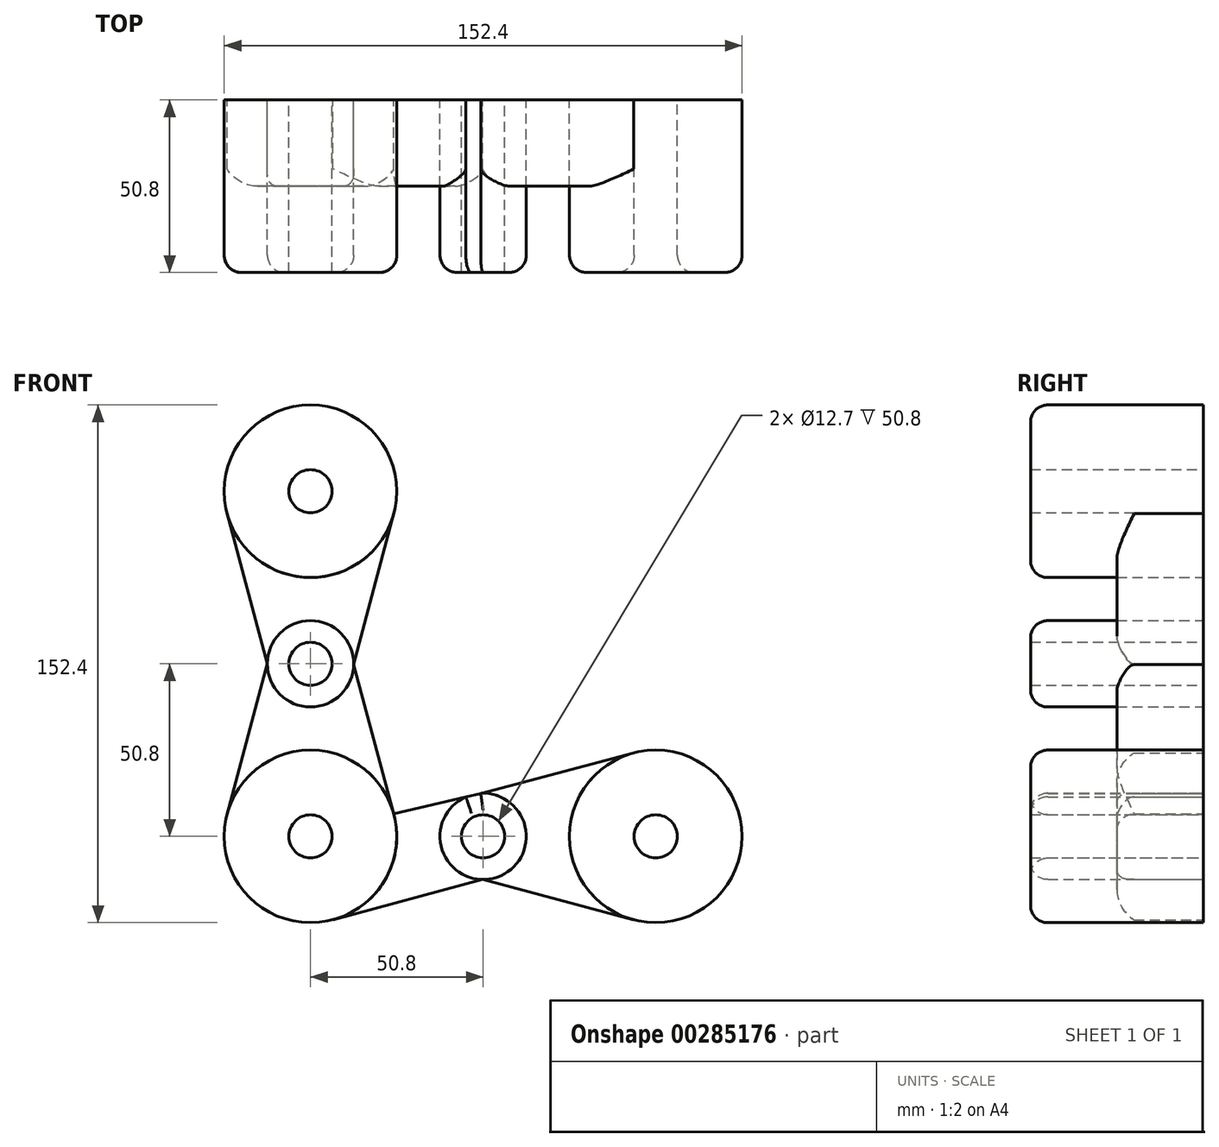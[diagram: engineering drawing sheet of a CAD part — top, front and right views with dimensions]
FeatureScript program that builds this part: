
annotation { "Feature Type Name" : "Feature", "Feature Type Description" : "" }
export const myFeature = defineFeature(function(context is Context, id is Id, definition is map)
    precondition{}
    {
        {
            var Q0;
            Q0=qCreatedBy(makeId("Front.planeOp"),FACE);
            var sketch = newSketch(context, id + "F0", { "sketchPlane" : qUnion([Q0])});
            skLineSegment(sketch, "E0", {"start": v(-86.7, -63.44) * mm, "end": v(-35.9, -63.44) * mm});
            skLineSegment(sketch, "E1", {"start": v(-35.9, -63.44) * mm, "end": v(14.9, -63.44) * mm});
            skPoint(sketch, "E1.endSnap0", {"position": v(-61.3, -63.44) * mm});
            skLineSegment(sketch, "E2", {"start": v(-86.7, -63.44) * mm, "end": v(-86.7, -12.64) * mm});
            skLineSegment(sketch, "E3", {"start": v(-86.7, -12.64) * mm, "end": v(-86.7, 38.16) * mm});
            skCircle(sketch, "E4", {"center": v(-86.7, 38.16) * mm, "radius": 25.4 * mm});
            skCircle(sketch, "E5", {"center": v(-86.7, -63.44) * mm, "radius": 25.4 * mm});
            skCircle(sketch, "E6", {"center": v(14.9, -63.44) * mm, "radius": 25.4 * mm});
            skCircle(sketch, "E7", {"center": v(-86.7, -12.64) * mm, "radius": 12.7 * mm});
            skCircle(sketch, "E8", {"center": v(-35.9, -63.44) * mm, "radius": 12.7 * mm});
            skLineSegment(sketch, "E9", {"start": v(-99.4, -12.64) * mm, "end": v(-111.23, -56.88) * mm});
            skLineSegment(sketch, "E10", {"start": v(-99.4, -12.64) * mm, "end": v(-111.23, 31.6) * mm});
            skLineSegment(sketch, "E11", {"start": v(-74, -12.86) * mm, "end": v(-62.17, -56.84) * mm});
            skLineSegment(sketch, "E12", {"start": v(-36.03, -76.14) * mm, "end": v(-80.1, -87.97) * mm});
            skLineSegment(sketch, "E13", {"start": v(-36.03, -76.14) * mm, "end": v(8.36, -87.98) * mm});
            skLineSegment(sketch, "E14", {"start": v(-74, -12.86) * mm, "end": v(-62.15, 31.62) * mm});
            skLineSegment(sketch, "E15", {"start": v(-36.6, -50.76) * mm, "end": v(8.43, -38.88) * mm});
            skLineSegment(sketch, "E16", {"start": v(-62.17, -56.84) * mm, "end": v(-36.6, -50.76) * mm});
            skSolve(sketch);
        }
        {
            var Q0;
            {var subQ0=sQuery(id+"F0.wireOp",EDGE,"E4");var subQ1=makeQuery(id+"F0.imprint","INTERSECT",VERTEX,{"derivedFrom":[subQ0,sQuery(id+"F0.wireOp",EDGE,"E10")]});Q0=makeQuery(id+"F0.imprint","IMPRINT",FACE,{"disambiguationData":[TD([[makeQuery(id+"F0.imprint","IMPRINT",EDGE,{"disambiguationData":[TD([[subQ1,-1.0]])],"derivedFrom":subQ0}),1.0]])]});}
            var Q1;
            {var subQ0=sQuery(id+"F0.wireOp",EDGE,"E3");var subQ1=sQuery(id+"F0.wireOp",EDGE,"E2");var subQ2=makeQuery(id+"F0.imprint","INTERSECT",VERTEX,{"derivedFrom":[subQ1,subQ0]});Q1=makeQuery(id+"F0.imprint","IMPRINT",FACE,{"disambiguationData":[TD([[makeQuery(id+"F0.imprint","IMPRINT",EDGE,{"disambiguationData":[TD([[subQ2,1.0]])],"derivedFrom":subQ1}),-1.0]])]});}
            var Q2;
            {var subQ0=sQuery(id+"F0.wireOp",EDGE,"E3");var subQ1=sQuery(id+"F0.wireOp",EDGE,"E2");var subQ2=makeQuery(id+"F0.imprint","INTERSECT",VERTEX,{"derivedFrom":[subQ1,subQ0]});Q2=makeQuery(id+"F0.imprint","IMPRINT",FACE,{"disambiguationData":[TD([[makeQuery(id+"F0.imprint","IMPRINT",EDGE,{"disambiguationData":[TD([[subQ2,1.0]])],"derivedFrom":subQ1}),1.0]])]});}
            var Q3;
            {var subQ3=sQuery(id+"F0.wireOp",EDGE,"E2");var subQ4=sQuery(id+"F0.wireOp",EDGE,"E0");var subQ5=makeQuery(id+"F0.imprint","INTERSECT",VERTEX,{"derivedFrom":[subQ4,subQ3]});Q3=makeQuery(id+"F0.imprint","IMPRINT",FACE,{"disambiguationData":[TD([[makeQuery(id+"F0.imprint","IMPRINT",EDGE,{"disambiguationData":[TD([[subQ5,-1.0]])],"derivedFrom":subQ4}),-1.0]])]});}
            var Q4;
            {var subQ0=sQuery(id+"F0.wireOp",EDGE,"E2");var subQ1=sQuery(id+"F0.wireOp",EDGE,"E0");var subQ2=makeQuery(id+"F0.imprint","INTERSECT",VERTEX,{"derivedFrom":[subQ1,subQ0]});Q4=makeQuery(id+"F0.imprint","IMPRINT",FACE,{"disambiguationData":[TD([[makeQuery(id+"F0.imprint","IMPRINT",EDGE,{"disambiguationData":[TD([[subQ2,-1.0]])],"derivedFrom":subQ1}),1.0]])]});}
            var Q5;
            {var subQ3=sQuery(id+"F0.wireOp",EDGE,"E1");var subQ5=sQuery(id+"F0.wireOp",EDGE,"E0");var subQ6=makeQuery(id+"F0.imprint","INTERSECT",VERTEX,{"derivedFrom":[subQ5,subQ3]});Q5=makeQuery(id+"F0.imprint","IMPRINT",FACE,{"disambiguationData":[TD([[makeQuery(id+"F0.imprint","IMPRINT",EDGE,{"disambiguationData":[TD([[subQ6,1.0]])],"derivedFrom":subQ5}),1.0]])]});}
            var Q6;
            {var subQ0=sQuery(id+"F0.wireOp",EDGE,"E1");var subQ1=sQuery(id+"F0.wireOp",EDGE,"E0");var subQ2=makeQuery(id+"F0.imprint","INTERSECT",VERTEX,{"derivedFrom":[subQ1,subQ0]});Q6=makeQuery(id+"F0.imprint","IMPRINT",FACE,{"disambiguationData":[TD([[makeQuery(id+"F0.imprint","IMPRINT",EDGE,{"disambiguationData":[TD([[subQ2,1.0]])],"derivedFrom":subQ1}),-1.0]])]});}
            var Q7;
            {var subQ0=sQuery(id+"F0.wireOp",EDGE,"E6");var subQ1=makeQuery(id+"F0.imprint","INTERSECT",VERTEX,{"derivedFrom":[subQ0,sQuery(id+"F0.wireOp",EDGE,"E15")]});Q7=makeQuery(id+"F0.imprint","IMPRINT",FACE,{"disambiguationData":[TD([[makeQuery(id+"F0.imprint","IMPRINT",EDGE,{"disambiguationData":[TD([[subQ1,-1.0]])],"derivedFrom":subQ0}),1.0]])]});}
            extrude(context, id + "F1", {"entities" : qUnion([Q0, Q1, Q2, Q3, Q4, Q5, Q6, Q7]), "depth" : 50.8 * mm});
        }
        {
            var Q0;
            {var subQ5=sQuery(id+"F0.wireOp",EDGE,"E10");Q0=makeQuery(id+"F0.imprint","IMPRINT",FACE,{"disambiguationData":[TD([[makeQuery(id+"F0.imprint","IMPRINT",EDGE,{"derivedFrom":subQ5}),-1.0]])]});}
            var Q1;
            {var subQ5=sQuery(id+"F0.wireOp",EDGE,"E14");Q1=makeQuery(id+"F0.imprint","IMPRINT",FACE,{"disambiguationData":[TD([[makeQuery(id+"F0.imprint","IMPRINT",EDGE,{"derivedFrom":subQ5}),1.0]])]});}
            var Q2;
            {var subQ5=sQuery(id+"F0.wireOp",EDGE,"E9");Q2=makeQuery(id+"F0.imprint","IMPRINT",FACE,{"disambiguationData":[TD([[makeQuery(id+"F0.imprint","IMPRINT",EDGE,{"derivedFrom":subQ5}),1.0]])]});}
            var Q3;
            {var subQ5=sQuery(id+"F0.wireOp",EDGE,"E11");Q3=makeQuery(id+"F0.imprint","IMPRINT",FACE,{"disambiguationData":[TD([[makeQuery(id+"F0.imprint","IMPRINT",EDGE,{"derivedFrom":subQ5}),-1.0]])]});}
            var Q4;
            {var subQ0=sQuery(id+"F0.wireOp",EDGE,"E5");var subQ1=sQuery(id+"F0.wireOp",EDGE,"E0");var subQ2=makeQuery(id+"F0.imprint","INTERSECT",VERTEX,{"derivedFrom":[subQ1,subQ0]});Q4=makeQuery(id+"F0.imprint","IMPRINT",FACE,{"disambiguationData":[TD([[makeQuery(id+"F0.imprint","IMPRINT",EDGE,{"disambiguationData":[TD([[subQ2,-1.0]])],"derivedFrom":subQ1}),1.0]])]});}
            var Q5;
            {var subQ5=sQuery(id+"F0.wireOp",EDGE,"E12");Q5=makeQuery(id+"F0.imprint","IMPRINT",FACE,{"disambiguationData":[TD([[makeQuery(id+"F0.imprint","IMPRINT",EDGE,{"derivedFrom":subQ5}),-1.0]])]});}
            var Q6;
            {var subQ5=sQuery(id+"F0.wireOp",EDGE,"E15");Q6=makeQuery(id+"F0.imprint","IMPRINT",FACE,{"disambiguationData":[TD([[makeQuery(id+"F0.imprint","IMPRINT",EDGE,{"derivedFrom":subQ5}),-1.0]])]});}
            var Q7;
            {var subQ5=sQuery(id+"F0.wireOp",EDGE,"E13");Q7=makeQuery(id+"F0.imprint","IMPRINT",FACE,{"disambiguationData":[TD([[makeQuery(id+"F0.imprint","IMPRINT",EDGE,{"derivedFrom":subQ5}),1.0]])]});}
            extrude(context, id + "F2", {"entities" : qUnion([Q0, Q1, Q2, Q3, Q4, Q5, Q6, Q7]), "depth" : 25.4 * mm});
        }
        {
            var Q0;
            Q0=sQuery(id+"F0.wireOp",VERTEX,"E4.center");
            var Q1;
            Q1=makeQuery(id+"F1.opExtrude","SWEPT_BODY",BODY,{"disambiguationData":[OSD([sQuery(id+"F0.wireOp",EDGE,"E4")])]});
            hole(context, id + "F3", {"style" : HoleStyle.SIMPLE, "endStyle" : HoleEndStyle.THROUGH, "oppositeDirection" : true, "holeDiameter" : 12.7 * mm, "tappedDepth" : 12.7 * mm, "tapClearance" : 3, "locations" : qUnion([Q0]), "scope" : qUnion([Q1])});
        }
        {
            var Q0;
            Q0=sQuery(id+"F0.wireOp",VERTEX,"E7.center");
            var Q1;
            Q1=makeQuery(id+"F1.opExtrude","SWEPT_BODY",BODY,{"disambiguationData":[OSD([sQuery(id+"F0.wireOp",EDGE,"E7")])]});
            hole(context, id + "F4", {"style" : HoleStyle.SIMPLE, "endStyle" : HoleEndStyle.THROUGH, "oppositeDirection" : true, "holeDiameter" : 12.7 * mm, "tappedDepth" : 12.7 * mm, "tapClearance" : 3, "locations" : qUnion([Q0]), "scope" : qUnion([Q1])});
        }
        {
            var Q0;
            Q0=sQuery(id+"F0.wireOp",VERTEX,"E0.start");
            var Q1;
            Q1=makeQuery(id+"F1.opExtrude","SWEPT_BODY",BODY,{"disambiguationData":[OSD([sQuery(id+"F0.wireOp",EDGE,"E5")])]});
            hole(context, id + "F5", {"style" : HoleStyle.SIMPLE, "endStyle" : HoleEndStyle.THROUGH, "oppositeDirection" : true, "holeDiameter" : 12.7 * mm, "tappedDepth" : 12.7 * mm, "tapClearance" : 3, "locations" : qUnion([Q0]), "scope" : qUnion([Q1])});
        }
        {
            var Q0;
            Q0=sQuery(id+"F0.wireOp",VERTEX,"E8.center");
            var Q1;
            Q1=makeQuery(id+"F1.opExtrude","SWEPT_BODY",BODY,{"disambiguationData":[OSD([sQuery(id+"F0.wireOp",EDGE,"E8"),sQuery(id+"F0.wireOp",EDGE,"E16")])]});
            hole(context, id + "F6", {"style" : HoleStyle.SIMPLE, "endStyle" : HoleEndStyle.THROUGH, "oppositeDirection" : true, "holeDiameter" : 12.7 * mm, "tappedDepth" : 12.7 * mm, "tapClearance" : 3, "locations" : qUnion([Q0]), "scope" : qUnion([Q1])});
        }
        {
            var Q0;
            Q0=sQuery(id+"F0.wireOp",VERTEX,"E6.center");
            var Q1;
            Q1=makeQuery(id+"F1.opExtrude","SWEPT_BODY",BODY,{"disambiguationData":[OSD([sQuery(id+"F0.wireOp",EDGE,"E6")])]});
            hole(context, id + "F7", {"style" : HoleStyle.SIMPLE, "endStyle" : HoleEndStyle.THROUGH, "oppositeDirection" : true, "holeDiameter" : 12.7 * mm, "tappedDepth" : 12.7 * mm, "tapClearance" : 3, "locations" : qUnion([Q0]), "scope" : qUnion([Q1])});
        }
        {
            var Q0;
            Q0=makeQuery(id+"F1.opExtrude","CAP_EDGE",EDGE,{"disambiguationData":[OSD([sQuery(id+"F0.wireOp",EDGE,"E4")])],"isStart":false});
            var Q1;
            Q1=makeQuery(id+"F1.opExtrude","CAP_EDGE",EDGE,{"disambiguationData":[OSD([sQuery(id+"F0.wireOp",EDGE,"E7")])],"isStart":false});
            var Q2;
            Q2=makeQuery(id+"F1.opExtrude","CAP_EDGE",EDGE,{"disambiguationData":[OSD([sQuery(id+"F0.wireOp",EDGE,"E5")])],"isStart":false});
            var Q3;
            Q3=makeQuery(id+"F1.opExtrude","CAP_EDGE",EDGE,{"disambiguationData":[OSD([sQuery(id+"F0.wireOp",EDGE,"E8")])],"isStart":false});
            var Q4;
            Q4=makeQuery(id+"F1.opExtrude","CAP_EDGE",EDGE,{"disambiguationData":[OSD([sQuery(id+"F0.wireOp",EDGE,"E16")])],"isStart":false});
            var Q5;
            Q5=makeQuery(id+"F1.opExtrude","CAP_FACE",FACE,{"disambiguationData":[OSD([sQuery(id+"F0.wireOp",EDGE,"E6")])],"isStart":false});
            var Q6;
            Q6=makeQuery(id+"F2.opExtrude","CAP_EDGE",EDGE,{"disambiguationData":[OSD([sQuery(id+"F0.wireOp",EDGE,"E13")])],"isStart":false});
            var Q7;
            Q7=makeQuery(id+"F2.opExtrude","CAP_EDGE",EDGE,{"disambiguationData":[OSD([sQuery(id+"F0.wireOp",EDGE,"E12")])],"isStart":false});
            var Q8;
            Q8=makeQuery(id+"F2.opExtrude","CAP_EDGE",EDGE,{"disambiguationData":[OSD([sQuery(id+"F0.wireOp",EDGE,"E10")])],"isStart":false});
            var Q9;
            Q9=makeQuery(id+"F2.opExtrude","CAP_EDGE",EDGE,{"disambiguationData":[OSD([sQuery(id+"F0.wireOp",EDGE,"E14")])],"isStart":false});
            var Q10;
            Q10=makeQuery(id+"F2.opExtrude","CAP_EDGE",EDGE,{"disambiguationData":[OSD([sQuery(id+"F0.wireOp",EDGE,"E11")])],"isStart":false});
            var Q11;
            Q11=makeQuery(id+"F2.opExtrude","CAP_EDGE",EDGE,{"disambiguationData":[OSD([sQuery(id+"F0.wireOp",EDGE,"E9")])],"isStart":false});
            var Q12;
            Q12=makeQuery(id+"F2.opExtrude","CAP_EDGE",EDGE,{"disambiguationData":[OSD([sQuery(id+"F0.wireOp",EDGE,"E15")])],"isStart":false});
            var Q13;
            Q13=makeQuery(id+"F2.opExtrude","CAP_EDGE",EDGE,{"disambiguationData":[OSD([sQuery(id+"F0.wireOp",EDGE,"E16")])],"isStart":false});
            var Q14;
            Q14=makeQuery(id+"F3.hole-0.boolean.opBoolean","INTERSECT",EDGE,{"derivedFrom":[makeQuery(id+"F1.opExtrude","CAP_FACE",FACE,{"disambiguationData":[OSD([sQuery(id+"F0.wireOp",EDGE,"E4")])],"isStart":false}),makeQuery(id+"F3.hole-0.opRevolve","SWEPT_FACE",FACE,{"disambiguationData":[OSD([sQuery(id+"F3.hole-0.sketch.wireOp",EDGE,"core_line_2")])]})]});
            var Q15;
            Q15=makeQuery(id+"F5.hole-0.boolean.opBoolean","INTERSECT",EDGE,{"derivedFrom":[makeQuery(id+"F1.opExtrude","CAP_FACE",FACE,{"disambiguationData":[OSD([sQuery(id+"F0.wireOp",EDGE,"E5")])],"isStart":false}),makeQuery(id+"F5.hole-0.opRevolve","SWEPT_FACE",FACE,{"disambiguationData":[OSD([sQuery(id+"F5.hole-0.sketch.wireOp",EDGE,"core_line_2")])]})]});
            fillet(context, id + "F8", {"entities" : qUnion([Q0, Q1, Q2, Q3, Q4, Q5, Q6, Q7, Q8, Q9, Q10, Q11, Q12, Q13, Q14, Q15]), "radius" : 5.08 * mm, "tangentPropagation" : true, "allowEdgeOverflow" : false});
        }
    });
